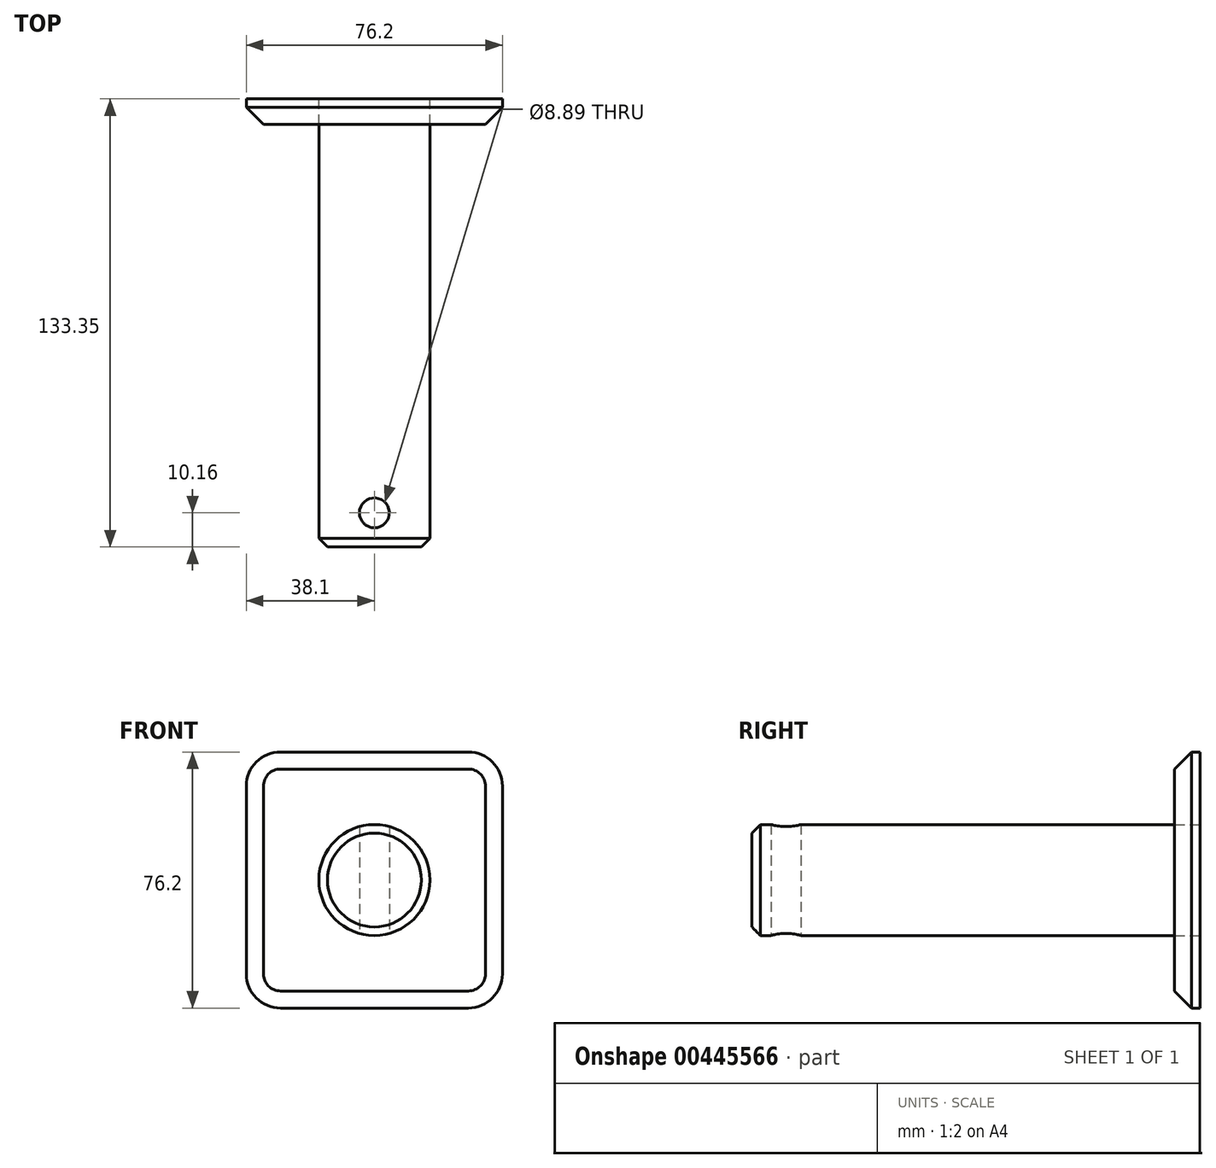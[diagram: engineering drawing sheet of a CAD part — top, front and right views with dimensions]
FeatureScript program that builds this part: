
annotation { "Feature Type Name" : "Feature", "Feature Type Description" : "" }
export const myFeature = defineFeature(function(context is Context, id is Id, definition is map)
    precondition{}
    {
        {
            var Q0;
            Q0=qCreatedBy(makeId("Front.planeOp"),FACE);
            var sketch = newSketch(context, id + "F0", { "sketchPlane" : qUnion([Q0])});
            skLineSegment(sketch, "E0.bottom", {"start": v(0, 0) * mm, "end": v(0, 0) * mm});
            skLineSegment(sketch, "E0.top", {"start": v(0, 76.2) * mm, "end": v(0, 76.2) * mm});
            skLineSegment(sketch, "E0.left", {"start": v(0, 0) * mm, "end": v(0, 76.2) * mm});
            skLineSegment(sketch, "E1.bottom", {"start": v(0, 76.2) * mm, "end": v(76.2, 76.2) * mm});
            skLineSegment(sketch, "E1.right", {"start": v(76.2, 76.2) * mm, "end": v(76.2, 76.2) * mm});
            skLineSegment(sketch, "E2.top", {"start": v(76.2, 0) * mm, "end": v(76.2, 0) * mm});
            skLineSegment(sketch, "E2.left", {"start": v(76.2, 76.2) * mm, "end": v(76.2, 0) * mm});
            skLineSegment(sketch, "E2.right", {"start": v(76.2, 76.2) * mm, "end": v(76.2, 0) * mm});
            skLineSegment(sketch, "E3.bottom", {"start": v(76.2, 0) * mm, "end": v(0, 0) * mm});
            skLineSegment(sketch, "E3.top", {"start": v(76.2, 0) * mm, "end": v(0, 0) * mm});
            skCircle(sketch, "E4", {"center": v(38.1, 38.1) * mm, "radius": 16.51 * mm});
            skSolve(sketch);
        }
        {
            var Q0;
            Q0=makeQuery(id+"F0.imprint","IMPRINT",FACE,{"disambiguationData":[TD([[makeQuery(id+"F0.imprint","IMPRINT",EDGE,{"derivedFrom":sQuery(id+"F0.wireOp",EDGE,"E4")}),1.0]])]});
            var Q1;
            Q1=sQuery(id+"F0.wireOp",EDGE,"E4");
            extrude(context, id + "F1", {"entities" : qUnion([Q0]), "surfaceEntities" : qUnion([Q1]), "depth" : 133.35 * mm});
        }
        {
            var Q0;
            Q0=qCreatedBy(makeId("Front.planeOp"),FACE);
            var sketch = newSketch(context, id + "F2", { "sketchPlane" : qUnion([Q0])});
            skLineSegment(sketch, "E5.bottom", {"start": v(0, 76.2) * mm, "end": v(76.2, 76.2) * mm});
            skLineSegment(sketch, "E5.top", {"start": v(0, 0) * mm, "end": v(76.2, 0) * mm});
            skLineSegment(sketch, "E5.left", {"start": v(0, 76.2) * mm, "end": v(0, 0) * mm});
            skLineSegment(sketch, "E5.right", {"start": v(76.2, 76.2) * mm, "end": v(76.2, 0) * mm});
            skSolve(sketch);
        }
        {
            var Q0;
            Q0=makeQuery(id+"F2.imprint","IMPRINT",FACE,{"disambiguationData":[TD([[makeQuery(id+"F2.imprint","IMPRINT",EDGE,{"derivedFrom":sQuery(id+"F2.wireOp",EDGE,"E5.bottom")}),-1.0]])]});
            var Q1;
            Q1=sQuery(id+"F2.wireOp",EDGE,"E5.left");
            var Q2;
            Q2=sQuery(id+"F2.wireOp",EDGE,"E5.top");
            var Q3;
            Q3=sQuery(id+"F2.wireOp",EDGE,"E5.right");
            var Q4;
            Q4=sQuery(id+"F2.wireOp",EDGE,"E5.bottom");
            extrude(context, id + "F3", {"entities" : qUnion([Q0]), "surfaceEntities" : qUnion([Q1, Q2, Q3, Q4]), "depth" : 7.62 * mm});
        }
        {
            var Q0;
            Q0=makeQuery(id+"F3.opExtrude","SWEPT_EDGE",EDGE,{"disambiguationData":[OSD([sQuery(id+"F2.wireOp",EDGE,"E5.top"),sQuery(id+"F2.wireOp",EDGE,"E5.left")])]});
            fillet(context, id + "F4", {"entities" : qUnion([Q0]), "radius" : 10.16 * mm, "tangentPropagation" : true, "allowEdgeOverflow" : false});
        }
        {
            var Q0;
            Q0=makeQuery(id+"F3.opExtrude","SWEPT_EDGE",EDGE,{"disambiguationData":[OSD([sQuery(id+"F2.wireOp",EDGE,"E5.top"),sQuery(id+"F2.wireOp",EDGE,"E5.right")])]});
            fillet(context, id + "F5", {"entities" : qUnion([Q0]), "radius" : 10.16 * mm, "tangentPropagation" : true, "allowEdgeOverflow" : false});
        }
        {
            var Q0;
            Q0=makeQuery(id+"F3.opExtrude","SWEPT_EDGE",EDGE,{"disambiguationData":[OSD([sQuery(id+"F2.wireOp",EDGE,"E5.bottom"),sQuery(id+"F2.wireOp",EDGE,"E5.left")])]});
            fillet(context, id + "F6", {"entities" : qUnion([Q0]), "radius" : 10.16 * mm, "tangentPropagation" : true, "allowEdgeOverflow" : false});
        }
        {
            var Q0;
            Q0=makeQuery(id+"F3.opExtrude","SWEPT_EDGE",EDGE,{"disambiguationData":[OSD([sQuery(id+"F2.wireOp",EDGE,"E5.bottom"),sQuery(id+"F2.wireOp",EDGE,"E5.right")])]});
            fillet(context, id + "F7", {"entities" : qUnion([Q0]), "radius" : 10.16 * mm, "tangentPropagation" : true, "allowEdgeOverflow" : false});
        }
        {
            var Q0;
            Q0=makeQuery(id+"F3.opExtrude","CAP_EDGE",EDGE,{"disambiguationData":[OSD([sQuery(id+"F2.wireOp",EDGE,"E5.top")])],"isStart":false});
            chamfer(context, id + "F8", {"entities" : qUnion([Q0]), "width" : 5.08 * mm, "tangentPropagation" : true});
        }
        {
            var Q0;
            Q0=makeQuery(id+"F1.opExtrude","CAP_EDGE",EDGE,{"disambiguationData":[OSD([sQuery(id+"F0.wireOp",EDGE,"E4")])],"isStart":false});
            chamfer(context, id + "F9", {"entities" : qUnion([Q0]), "width" : 2.54 * mm, "tangentPropagation" : true});
        }
        {
            var Q0;
            Q0=qCreatedBy(makeId("Top.planeOp"),FACE);
            var sketch = newSketch(context, id + "F10", { "sketchPlane" : qUnion([Q0])});
            skCircle(sketch, "E6", {"center": v(38.1, -123.2) * mm, "radius": 4.45 * mm});
            skSolve(sketch);
        }
        {
            var Q0;
            Q0=makeQuery(id+"F10.imprint","IMPRINT",FACE,{"disambiguationData":[TD([[makeQuery(id+"F10.imprint","IMPRINT",EDGE,{"derivedFrom":sQuery(id+"F10.wireOp",EDGE,"E6")}),1.0]])]});
            var Q1;
            Q1=sQuery(id+"F10.wireOp",EDGE,"E6");
            extrude(context, id + "F11", {"entities" : qUnion([Q0]), "operationType" : NewBodyOperationType.REMOVE, "surfaceEntities" : qUnion([Q1]), "oppositeDirection" : true, "depth" : -76.2 * mm});
        }
    });
